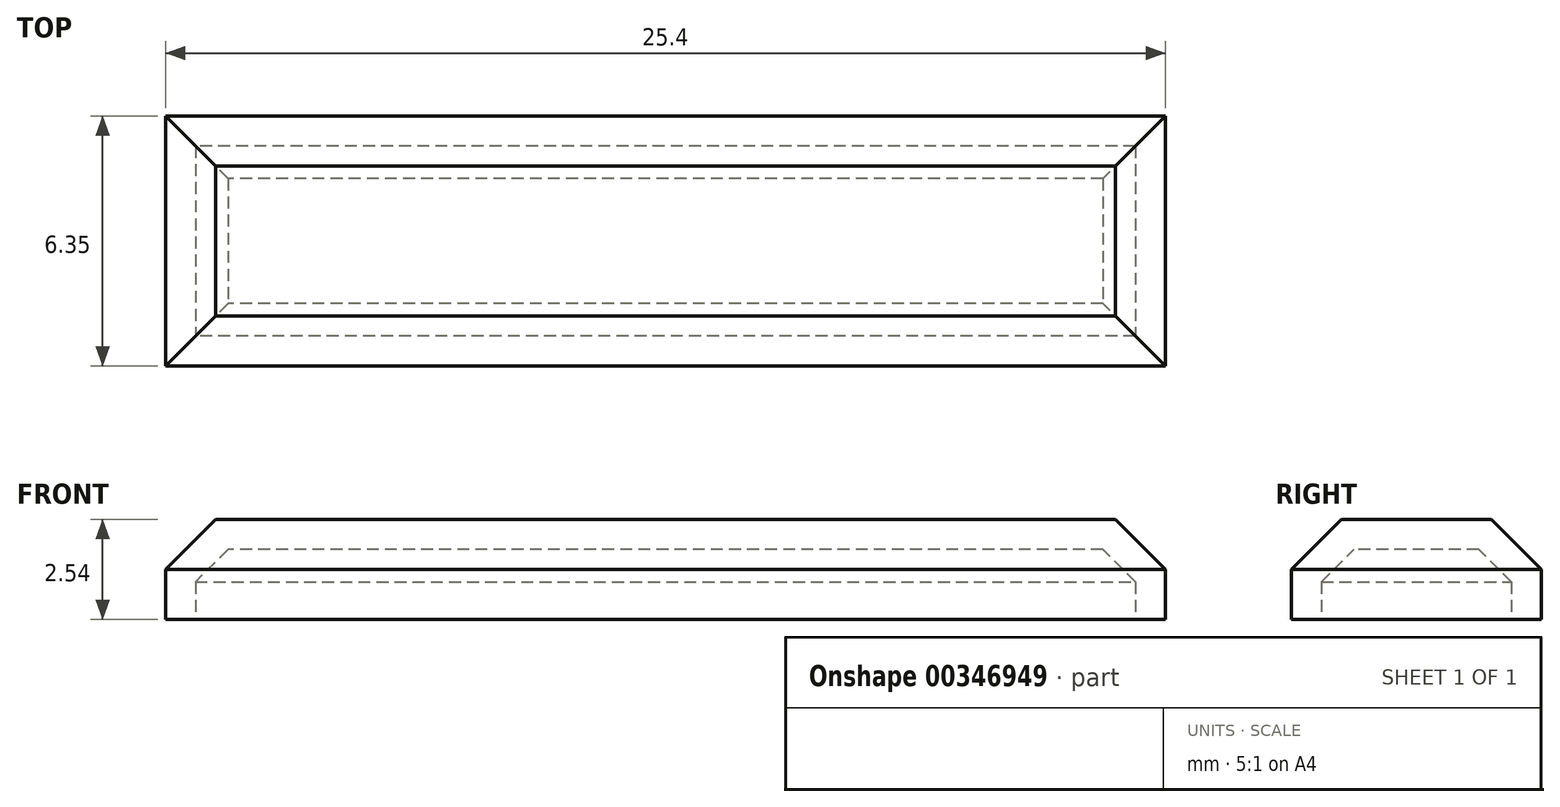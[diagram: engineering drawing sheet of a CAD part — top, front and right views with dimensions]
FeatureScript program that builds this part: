
annotation { "Feature Type Name" : "Feature", "Feature Type Description" : "" }
export const myFeature = defineFeature(function(context is Context, id is Id, definition is map)
    precondition{}
    {
        {
            var Q0;
            Q0=qCreatedBy(makeId("Top.planeOp"),FACE);
            var sketch = newSketch(context, id + "F0", { "sketchPlane" : qUnion([Q0])});
            skLineSegment(sketch, "E0.bottom", {"start": v(-41.66, -49.27) * mm, "end": v(-67.06, -49.27) * mm});
            skLineSegment(sketch, "E0.top", {"start": v(-41.66, -55.62) * mm, "end": v(-67.06, -55.62) * mm});
            skLineSegment(sketch, "E0.left", {"start": v(-41.66, -49.27) * mm, "end": v(-41.66, -55.62) * mm});
            skLineSegment(sketch, "E0.right", {"start": v(-67.06, -49.27) * mm, "end": v(-67.06, -55.62) * mm});
            skSolve(sketch);
        }
        {
            var Q0;
            Q0=makeQuery(id+"F0.imprint","IMPRINT",FACE,{"disambiguationData":[TD([[makeQuery(id+"F0.imprint","IMPRINT",EDGE,{"derivedFrom":sQuery(id+"F0.wireOp",EDGE,"E0.bottom")}),1.0]])]});
            extrude(context, id + "F1", {"entities" : qUnion([Q0]), "depth" : 2.54 * mm});
        }
        {
            var Q0;
            Q0=makeQuery(id+"F1.opExtrude","CAP_FACE",FACE,{"disambiguationData":[OSD([sQuery(id+"F0.wireOp",EDGE,"E0.bottom"),sQuery(id+"F0.wireOp",EDGE,"E0.top"),sQuery(id+"F0.wireOp",EDGE,"E0.left"),sQuery(id+"F0.wireOp",EDGE,"E0.right")])],"isStart":false});
            chamfer(context, id + "F2", {"entities" : qUnion([Q0]), "width" : 1.27 * mm, "tangentPropagation" : true});
        }
        {
            var Q0;
            Q0=makeQuery(id+"F1.opExtrude","CAP_FACE",FACE,{"disambiguationData":[OSD([sQuery(id+"F0.wireOp",EDGE,"E0.bottom"),sQuery(id+"F0.wireOp",EDGE,"E0.top"),sQuery(id+"F0.wireOp",EDGE,"E0.left"),sQuery(id+"F0.wireOp",EDGE,"E0.right")])],"isStart":true});
            shell(context, id + "F3", {"entities" : qUnion([Q0]), "thickness" : 0.76 * mm});
        }
    });
